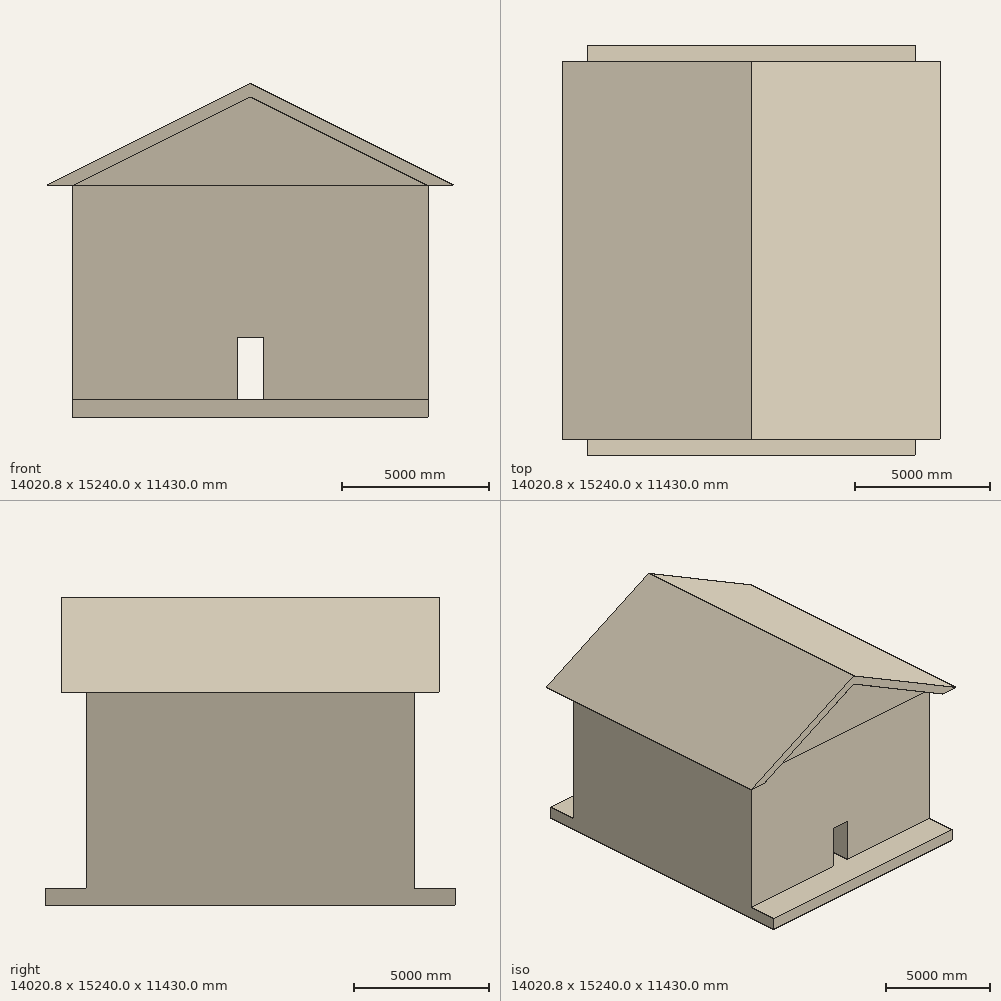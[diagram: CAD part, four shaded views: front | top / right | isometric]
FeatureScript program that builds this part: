
annotation { "Feature Type Name" : "Feature", "Feature Type Description" : "" }
export const myFeature = defineFeature(function(context is Context, id is Id, definition is map)
    precondition{}
    {
        {
            var Q0;
            Q0=qCreatedBy(makeId("Front.planeOp"),FACE);
            var sketch = newSketch(context, id + "F0", { "sketchPlane" : qUnion([Q0])});
            skLineSegment(sketch, "E0", {"start": v(0, 0) * mm, "end": v(-6096, 0) * mm});
            skLineSegment(sketch, "E1", {"start": v(0, 0) * mm, "end": v(6096, 0) * mm});
            skLineSegment(sketch, "E2", {"start": v(0, 0) * mm, "end": v(0, 3048) * mm});
            skLineSegment(sketch, "E3", {"start": v(0, 3048) * mm, "end": v(6096, 0) * mm});
            skLineSegment(sketch, "E4", {"start": v(-6096, 0) * mm, "end": v(-6096, -7315.2) * mm});
            skLineSegment(sketch, "E5", {"start": v(6096, 0) * mm, "end": v(6096, -7315.2) * mm});
            skLineSegment(sketch, "E6", {"start": v(-6096, -7315.2) * mm, "end": v(6096, -7315.2) * mm});
            skLineSegment(sketch, "E7", {"start": v(-6096, 0) * mm, "end": v(0, 3048) * mm});
            skLineSegment(sketch, "E8", {"start": v(-6096, -7315.2) * mm, "end": v(-6096, -7924.8) * mm});
            skLineSegment(sketch, "E9", {"start": v(6096, -7315.2) * mm, "end": v(6096, -7924.8) * mm});
            skLineSegment(sketch, "E10", {"start": v(6096, -7924.8) * mm, "end": v(-6096, -7924.8) * mm});
            skLineSegment(sketch, "E11", {"start": v(0, -7315.2) * mm, "end": v(-457.2, -7315.2) * mm});
            skLineSegment(sketch, "E12", {"start": v(0, -7315.2) * mm, "end": v(457.2, -7315.2) * mm});
            skLineSegment(sketch, "E13", {"start": v(457.2, -7315.2) * mm, "end": v(457.2, -5181.6) * mm});
            skLineSegment(sketch, "E14", {"start": v(-457.2, -7315.2) * mm, "end": v(-457.2, -5181.6) * mm});
            skLineSegment(sketch, "E15", {"start": v(457.2, -5181.6) * mm, "end": v(-457.2, -5181.6) * mm});
            skLineSegment(sketch, "E16", {"start": v(-6096, 0) * mm, "end": v(-7010.4, 0) * mm});
            skLineSegment(sketch, "E17", {"start": v(6096, 0) * mm, "end": v(7010.4, 0) * mm});
            skLineSegment(sketch, "E18", {"start": v(0, 3048) * mm, "end": v(0, 3505.2) * mm});
            skLineSegment(sketch, "E19", {"start": v(0, 3505.2) * mm, "end": v(7010.4, 0) * mm});
            skLineSegment(sketch, "E20", {"start": v(0, 3505.2) * mm, "end": v(-7010.4, 0) * mm});
            skSolve(sketch);
        }
        {
            var Q0;
            Q0=makeQuery(id+"F0.imprint","IMPRINT",FACE,{"disambiguationData":[TD([[makeQuery(id+"F0.imprint","IMPRINT",EDGE,{"derivedFrom":sQuery(id+"F0.wireOp",EDGE,"E7")}),1.0]])]});
            var Q1;
            Q1=makeQuery(id+"F0.imprint","IMPRINT",FACE,{"disambiguationData":[TD([[makeQuery(id+"F0.imprint","IMPRINT",EDGE,{"derivedFrom":sQuery(id+"F0.wireOp",EDGE,"E3")}),1.0]])]});
            extrude(context, id + "F1", {"entities" : qUnion([Q0, Q1]), "endBound" : BoundingType.SYMMETRIC, "depth" : 14020.8 * mm, "offsetDistance" : 30.48 * mm});
        }
        {
            var Q0;
            Q0=makeQuery(id+"F0.imprint","IMPRINT",FACE,{"disambiguationData":[TD([[makeQuery(id+"F0.imprint","IMPRINT",EDGE,{"derivedFrom":sQuery(id+"F0.wireOp",EDGE,"E0")}),1.0]])]});
            extrude(context, id + "F2", {"entities" : qUnion([Q0]), "endBound" : BoundingType.SYMMETRIC, "depth" : 12192 * mm, "offsetDistance" : 30.48 * mm});
        }
        {
            var Q0;
            {var subQ1=sQuery(id+"F0.wireOp",EDGE,"E8");Q0=makeQuery(id+"F0.imprint","IMPRINT",FACE,{"disambiguationData":[TD([[makeQuery(id+"F0.imprint","IMPRINT",EDGE,{"derivedFrom":subQ1}),1.0]])]});}
            extrude(context, id + "F3", {"entities" : qUnion([Q0]), "operationType" : NewBodyOperationType.ADD, "endBound" : BoundingType.SYMMETRIC, "depth" : 15240 * mm, "offsetDistance" : 30.48 * mm});
        }
        {
            var Q0;
            Q0=makeQuery(id+"F0.imprint","IMPRINT",FACE,{"disambiguationData":[TD([[makeQuery(id+"F0.imprint","IMPRINT",EDGE,{"derivedFrom":sQuery(id+"F0.wireOp",EDGE,"E0")}),-1.0]])]});
            var Q1;
            Q1=makeQuery(id+"F0.imprint","IMPRINT",FACE,{"disambiguationData":[TD([[makeQuery(id+"F0.imprint","IMPRINT",EDGE,{"derivedFrom":sQuery(id+"F0.wireOp",EDGE,"E1")}),1.0]])]});
            extrude(context, id + "F4", {"entities" : qUnion([Q0, Q1]), "endBound" : BoundingType.SYMMETRIC, "depth" : 12496.8 * mm, "offsetDistance" : 30.48 * mm});
        }
    });
